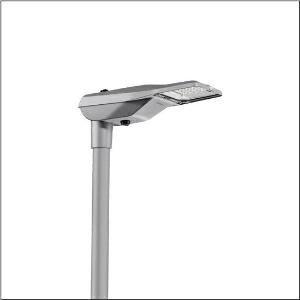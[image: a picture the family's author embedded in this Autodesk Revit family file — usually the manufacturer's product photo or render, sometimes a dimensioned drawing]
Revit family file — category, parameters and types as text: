
# Revit family: streetlight_sl_21_iq_micro___st0_8a_5xe1c31y08cb_ba99
name_source: partatom
category: Lighting Fixtures
units: mm (PartAtom-declared; Revit-internal decimal feet)

## family parameters
Cut with Voids When Loaded = No
Host = Face
Light Source = No
Part Type = Normal
Room Calculation Point = No
Round Connector Dimension = Use Diameter
Shared = No

## types (1)
- --- (1 x LED, 2880 lm, 19.1 W, 3000K)
    Apparent Load = 19 VA
    CIE Flux Codes = 38 75 97 100 100
    Color Rendering = 70
    Color Temperature = 3000K
    Default Elevation = 1800 mm
    Description = Streetlight SL 21 iQ micro, mast luminaire, primary light control with lens, of PMMA, primary optical cover: cover, of toughened safety glass, transparent, light distribution: ST0.8a, light emission: direct distribution, primary light characteristic: asymmetric, installation type: post-top, side-entry, LED, High Power LED, rated luminous flux: 2.880lm, luminous efficacy: 151lm/W, light colour: 730, colour temperature: 3000K, control: presetting dimming logarithmic, Street-Remote, Auto-Match, Temp-Guard, Lumen-Switch, Night-Set, Smart-Wire, Light-Fading, Desk-Remote (wireless, voltage-free reading and setting of iQ features in the workshop via application-optimized NFC function/RFID function), optimised constant luminous flux control (CLO 2.0), mains connection: 220..240V, AC, 50/60Hz, start of lifetime: 19W, end of service life: 20W, reduction: 9W, luminaire housing, of diecast aluminium, powder-coated, Siteco® metallic grey (DB 702S), corrosivity category C5 mid according to DIN EN ISO 12944, please order mast flange separately, inclination adjustable: 0°, 5°, 10°, 15°, sealing non-destructively replaceable, multi-level sealing system, length: 528mm, width: 235mm, height: 110mm, mast flange for spigot size: 42mm (side-entry): 5XC10008XM4, 60/48mm (side-entry/post-top): 5XC10108XM2, 76/60mm (side-entry/post-top): 5XC10108XM1, Smart Interface below and above, protection rating (complete): IP66, insulation class (complete): insulation class II (safety insulation), certification: CE, ENEC, ENEC+, VDE, impact resistance: IK09, permissible operating ambient temperature for outdoor applications: -40..+50°C, standard-compliant lighting for roads and squares, packaging unit: 1 piece

Light Distribution: ST0.8a
    Height = 110 mm
    Lamp = 1 x LED
    Lamp Light Flux = 2880 lm
    Lamp Power = 19.1 W
    Lamp count = 1
    Length = 528 mm
    Luminous efficacy = 151 lm/W
    Manufacturer = Siteco
    ModVariant = No
    Model = 5XE1C31Y08CB
    Number of Poles = 1
    OnlyDefault = Yes
    Power Factor = 1
    Product Name = Streetlight SL 21 iQ micro | ST0.8a
    Product group = mast luminaire | pylon top
    ProductGroupID = 6100
    Protection Class = Protection class II
    Protection Degree = IP 66
    RLX_Detail_Level = 1
    RLX_Emergency_Light_Flux = 0 lm
    RLX_Emergency_Type = 0
    RLX_Emergency_Type_DB = No
    RlxData = <blob elided: 99093 chars, md5=ea44386b>
    Socket = socket
    Standby Power = 0 W
    System Light Flux = 2880 lm
    System Power = 19 W
    Type Comments = factory setting: luminous flux: 100 % | dim-lin: 254 | 387 mA
    Type Image = l_1007239.jpg
    URL = http://relux.com
    VarID = @adj_061621
    Voltage = 0 V
    Weight = 0.00 kg
    Width = 235 mm

## geometry (parser evidence)
native form markers: Blend x4, Sweep x10
no freeform markers — native parametric forms only
